# Revit family: Door_Overhead-Coiling_CHI_6200-Series
name_source: partatom
category: Doors
units: mm (PartAtom-declared; Revit-internal decimal feet)

## family parameters
Always vertical = Yes
Cut with Voids When Loaded = No
Host = Wall
OmniClass Number = 23.30.10.17.27.11
OmniClass Title = Overhead Coiling
Room Calculation Point = No
Shared = No

## types (6) — shared parameters
Analytic Construction = <None>
Assembly Code = B2030420
Body Material = Metal - CHI - Silver Powdercoat
Description = CHI Medium Duty Service Overhead Coiling Door - Model 6241
Fire Rating = As Specified in 08330
Frame Finish = Metal - CHI - Black Powdercoat
Function = Interior
Has Windlocks = No
Height = 9' - 2 1/2"
Keynote = 08330
Manufacturer = CHI Overhead Doors
Max Height = 14' - 4"
Max Width = 12' - 0"
Model = Model 6241
RO Offset = 0' - 0"
Revision = R1_02-2013
Rough Height = 9' - 3"
Rough Width = 9' - 1"
Thickness = 0' - 0 1/4"
URL = http://www.chiohd.com
Wall Closure = By host
Width = 9' - 0"
zero-valued in all types: Expected Lifespan (Years), Maintenance Schedule (Months), R_Value, Sound Transmission Class (STC), Warranty Duration (Years)

## per-type parameters (varying)
| type | Guide_E Guide | Guide_Z Guide | Voltage_MEP |
| Z Guide for Wood or Masonry Structure 440V | No | Yes | 440 V |
| Z Guide for Wood or Masonry Structure 220V | No | Yes | 220 V |
| Z Guide for Wood or Masonry Structure 115V | No | Yes | 115 V |
| E Guide for Steel Structure 440V | Yes | No | 440 V |
| E Guide for Steel Structure 220V | Yes | No | 220 V |
| E Guide for Steel Structure 115V | Yes | No | 115 V |

## geometry (parser evidence)
native form markers: Blend x4, Sweep x5
no freeform markers — native parametric forms only
